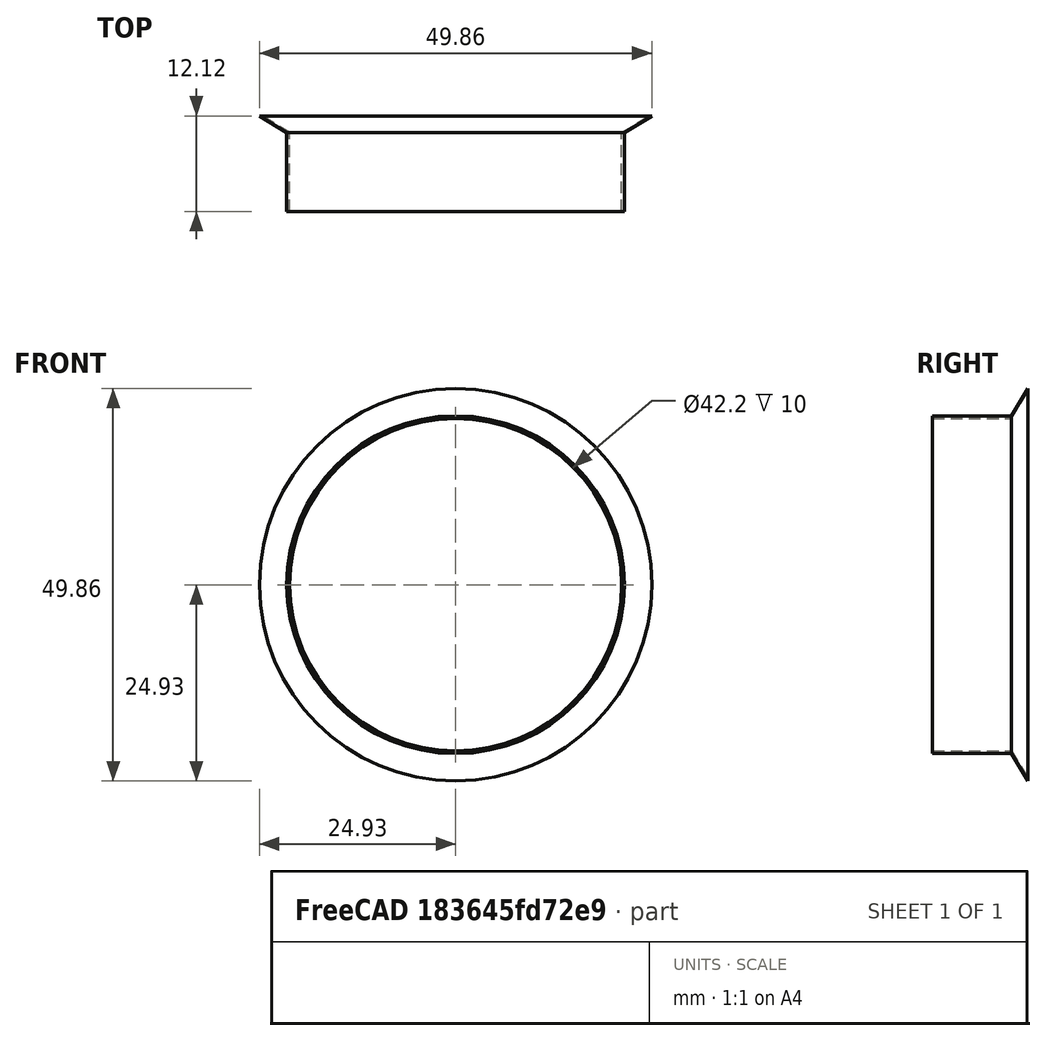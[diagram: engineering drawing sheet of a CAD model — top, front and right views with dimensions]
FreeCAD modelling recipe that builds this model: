
FCSTD DOCUMENT  (FreeCAD 0.17R13519 (Git))
Label: laserWelderRingV2
License: All rights reserved
LicenseURL: http://en.wikipedia.org/wiki/All_rights_reserved
objects: TechDraw::DrawViewDimension×8, TechDraw::DrawProjGroupItem×3, Sketcher::SketchObject×1, PartDesign::Revolution×1, PartDesign::Fillet×1, PartDesign::Body×1, TechDraw::DrawSVGTemplate×1, TechDraw::DrawProjGroup×1, TechDraw::DrawPage×1
note: 5 computed .brp shape members not serialized (recipe doc carries the construction recipe); baked Part::Feature solids carry a one-line shape summary decoded from their .brp

FEATURE [Sketcher::SketchObject] Sketch
  sketch-geometry (7):
    g0: GeomPoint X=0 Y=0 Z=0
    g1: LineSegment StartX=21.1 StartY=0 StartZ=0 EndX=21.1 EndY=10 EndZ=0
    g2: LineSegment StartX=21.1 StartY=10 StartZ=0 EndX=24.5797 EndY=12.1157 EndZ=0
    g3: LineSegment StartX=24.5797 StartY=12.1157 StartZ=0 EndX=24.9297 EndY=12.1157 EndZ=0
    g4: LineSegment StartX=24.9297 StartY=12.1157 StartZ=0 EndX=21.45 EndY=10 EndZ=0
    g5: LineSegment StartX=21.45 StartY=10 StartZ=0 EndX=21.45 EndY=0 EndZ=0
    g6: LineSegment StartX=21.45 StartY=0 StartZ=0 EndX=21.1 EndY=0 EndZ=0
  constraints (18):
    c: PointOnObject(g0,g-1)
    c: Vertical(g1)
    c: Coincident(g1,g2)
    c: Coincident(g2,g3)
    c: Coincident(g3,g4)
    c: Coincident(g4,g5)
    c: PointOnObject(g5,g-1)
    c: Vertical(g5)
    c: Coincident(g5,g6)
    c: Coincident(g6,g1)
    c: Horizontal(g6)
    c: DistanceX(g-1,g1) = 21.1
    c: DistanceX(g1,g5) = 0.35
    c: DistanceY(g1,g1) = 10
    c: DistanceY(g5,g5) = 10
    c: Angle(g5,g4) = 2.11708
    c: Angle(g1,g2) = 2.11708
    c: Horizontal(g3)
FEATURE [PartDesign::Revolution] Revolution
  Angle = 360
  Axis = (0,1,0)
  Base = (0,0,0)
  Profile = -> Sketch
  ReferenceAxis = -> Sketch [V_Axis]
  Refine = true
  Reversed = true
FEATURE [PartDesign::Fillet] Fillet
  Base = -> Revolution [Edge4]
  BaseFeature = -> Revolution
  Radius = 1
FEATURE [PartDesign::Body] Body
  Group = -> [Sketch,Revolution,Fillet]
  Origin = -> Origin
  Tip = -> Fillet
FEATURE [TechDraw::DrawProjGroupItem] ProjItem001  label="Top"
  CoarseView = false
  Direction = (0,0,1)
  Focus = 100
  HardHidden = false
  IsoCount = 0
  IsoHidden = false
  IsoVisible = false
  LockPosition = false
  Perspective = false
  Rotation = 0
  RotationVector = (1,0,0)
  ScaleType = 0
  SeamHidden = false
  SeamVisible = false
  SmoothHidden = false
  SmoothVisible = false
  Source = -> [Body]
  Type = 4
  X = 0
  Y = -64.761
FEATURE [TechDraw::DrawSVGTemplate] Template
  EditableTexts = AUTHOR_NAME=J LAU / J MILLER; DN=DN; DRAWING_TITLE=LASER WELD FOCUS RING; FC-DATE=1/08/2018; FC-REV=REV A; FC-SC=2:1; FC-SH=X / Y; FC-SI=A4; FreeCAD_DRAWING=Tolerance: 0.05; PN=PN; SI-1=Material: Titanium; SI-2=1 off; SI-4=All units mm
  Height = 297
  Orientation = 0
  Width = 210
FEATURE [TechDraw::DrawProjGroupItem] ProjItem  label="Front"
  CoarseView = true
  Direction = (0,-1,0)
  Focus = 100
  HardHidden = true
  IsoCount = 0
  IsoHidden = true
  IsoVisible = true
  LockPosition = false
  Perspective = false
  Rotation = 0
  RotationVector = (1,0,0)
  ScaleType = 0
  SeamHidden = true
  SeamVisible = true
  SmoothHidden = true
  SmoothVisible = true
  Source = -> [Body]
  Type = 0
  X = 0
  Y = 0
FEATURE [TechDraw::DrawProjGroupItem] ProjItem002  label="Top001"
  CoarseView = true
  Direction = (0,0,1)
  Focus = 100
  HardHidden = true
  IsoCount = 0
  IsoHidden = true
  IsoVisible = true
  LockPosition = false
  Perspective = false
  Rotation = 0
  RotationVector = (1,0,0)
  Scale = 2
  ScaleType = 2
  SeamHidden = true
  SeamVisible = true
  SmoothHidden = true
  SmoothVisible = true
  Source = -> [Body]
  Type = 4
  X = 0
  Y = -114.694
FEATURE [TechDraw::DrawProjGroup] ProjGroup
  Anchor = -> ProjItem
  AutoDistribute = true
  CubeDirs = (1) [(0,0,0)]
  CubeRotations = (1) [(0,0,0)]
  LockPosition = false
  ProjectionType = 0
  Rotation = 0
  Scale = 2
  ScaleType = 2
  Source = -> [Body]
  Views = -> [ProjItem,ProjItem002]
  X = 108.194
  Y = 235.305
  spacingX = 15
  spacingY = 15
FEATURE [TechDraw::DrawViewDimension] Dimension
  FormatSpec = %.2f
  LockPosition = false
  MeasureType = 1
  References2D = -> [ProjItem002]
  Rotation = 0
  ScaleType = 0
  Type = 6
  X = -68.0026
  Y = -5.82172
FEATURE [TechDraw::DrawViewDimension] Dimension001
  FormatSpec = %.2f
  LockPosition = false
  MeasureType = 1
  References2D = -> [ProjItem002]
  Rotation = 0
  ScaleType = 0
  Type = 2
  X = 60.0752
  Y = -7.18425
FEATURE [TechDraw::DrawViewDimension] Dimension002
  FormatSpec = %.2f
  LockPosition = false
  MeasureType = 1
  References2D = -> [ProjItem002]
  Rotation = 0
  ScaleType = 0
  Type = 2
  X = 63.5434
  Y = 13.6253
FEATURE [TechDraw::DrawViewDimension] Dimension003
  FormatSpec = %.2f
  LockPosition = false
  MeasureType = 1
  References2D = -> [ProjItem002]
  Rotation = 0
  ScaleType = 0
  Type = 1
  X = 45.9271
  Y = 34.3146
FEATURE [TechDraw::DrawViewDimension] Dimension004
  FormatSpec = %.2f
  LockPosition = false
  MeasureType = 1
  References2D = -> [ProjItem002]
  Rotation = 0
  ScaleType = 0
  Type = 1
  X = -0.316868
  Y = 20.7548
FEATURE [TechDraw::DrawViewDimension] Dimension005
  FormatSpec = %.2f
  LockPosition = false
  MeasureType = 1
  References2D = -> [ProjItem002]
  Rotation = 0
  ScaleType = 0
  Type = 1
  X = 0.633736
  Y = -28.5181
FEATURE [TechDraw::DrawViewDimension] Dimension006
  FormatSpec = %.2f
  LockPosition = false
  MeasureType = 1
  References2D = -> [ProjItem002]
  Rotation = 0
  ScaleType = 0
  Type = 1
  X = -31.4227
  Y = -37.364
FEATURE [TechDraw::DrawViewDimension] Dimension007
  FormatSpec = %.2f
  LockPosition = false
  MeasureType = 1
  References2D = -> [ProjItem]
  Rotation = 0
  ScaleType = 0
  Type = 1
  X = -0.14463
  Y = 3.905
FEATURE [TechDraw::DrawPage] Page
  KeepUpdated = true
  ProjectionType = 0
  Template = -> Template
  Views = -> [ProjGroup,Dimension,Dimension001,Dimension002,Dimension003,Dimension004,Dimension005,Dimension006,Dimension007]
